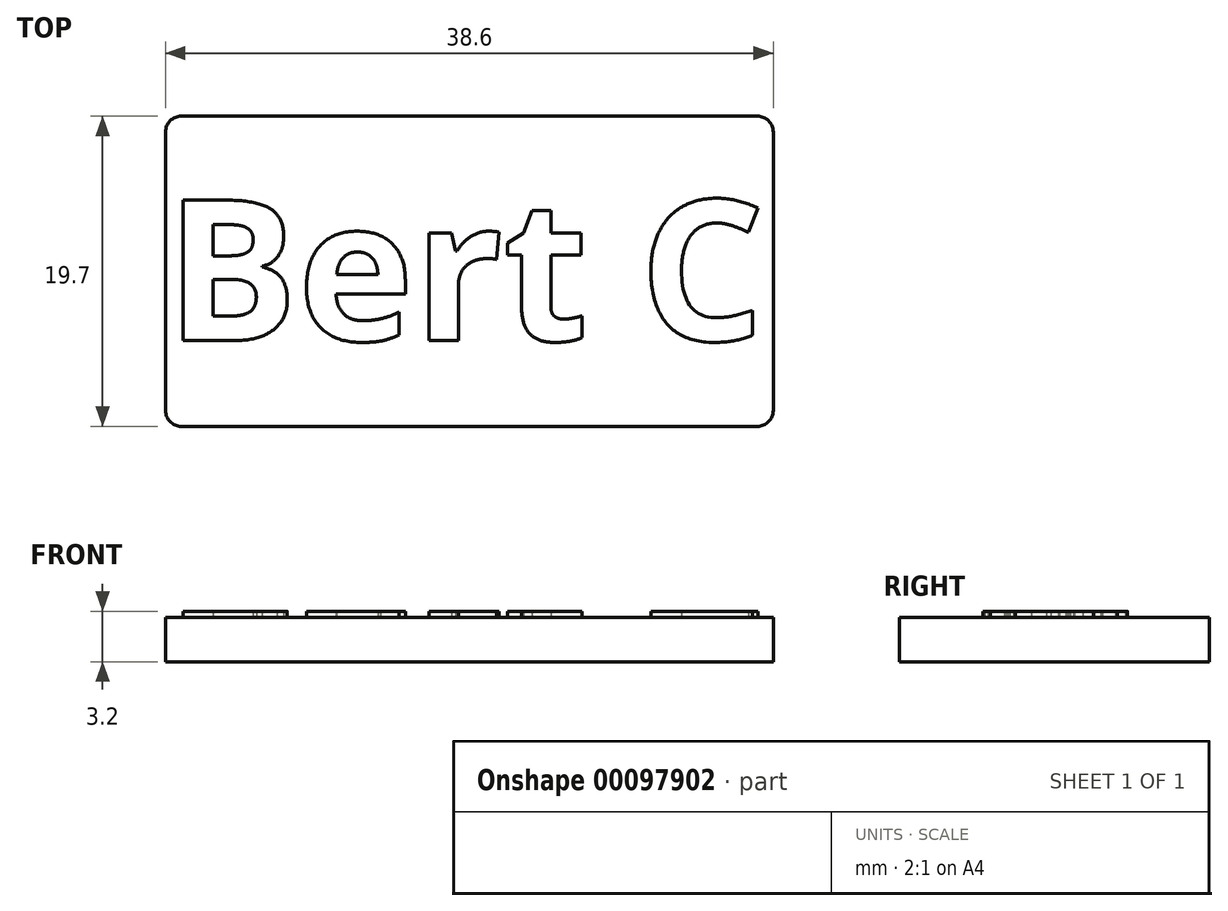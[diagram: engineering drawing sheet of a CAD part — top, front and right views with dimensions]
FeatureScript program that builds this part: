
annotation { "Feature Type Name" : "Feature", "Feature Type Description" : "" }
export const myFeature = defineFeature(function(context is Context, id is Id, definition is map)
    precondition{}
    {
        {
            var Q0;
            Q0=qCreatedBy(makeId("Top.planeOp"),FACE);
            var sketch = newSketch(context, id + "F0", { "sketchPlane" : qUnion([Q0])});
            skLineSegment(sketch, "E0.bottom", {"start": v(-23.84, 19.7) * mm, "end": v(14.76, 19.7) * mm});
            skLineSegment(sketch, "E0.top", {"start": v(-23.84, 0) * mm, "end": v(14.76, 0) * mm});
            skLineSegment(sketch, "E0.left", {"start": v(-23.84, 19.7) * mm, "end": v(-23.84, 0) * mm});
            skLineSegment(sketch, "E0.right", {"start": v(14.76, 19.7) * mm, "end": v(14.76, 0) * mm});
            skText(sketch, "E1", { "text": "Bert C\n", "fontName": "OpenSans-Bold.ttf"});
            const initialGuessF0  = {"E1": [-0.02384, 0.00545, 1, 0, 0.00899]};
            skSetInitialGuess(sketch, initialGuessF0);
            skSolve(sketch);
        }
        {
            var Q0;
            Q0=makeQuery(id+"F0.imprint","IMPRINT",FACE,{"disambiguationData":[TD([[makeQuery(id+"F0.imprint","IMPRINT",EDGE,{"derivedFrom":sQuery(id+"F0.wireOp",EDGE,"E0.bottom")}),-1.0]])]});
            var Q1;
            Q1=makeQuery(id+"F0.imprint","IMPRINT",FACE,{"disambiguationData":[TD([[makeQuery(id+"F0.imprint","IMPRINT",EDGE,{"derivedFrom":sQuery(id+"F0.wireOp",EDGE,"E1.sketch_text.stroke-0")}),-1.0]])]});
            var Q2;
            Q2=makeQuery(id+"F0.imprint","IMPRINT",FACE,{"disambiguationData":[TD([[makeQuery(id+"F0.imprint","IMPRINT",EDGE,{"derivedFrom":sQuery(id+"F0.wireOp",EDGE,"E1.sketch_text.stroke-12")}),1.0]])]});
            var Q3;
            Q3=makeQuery(id+"F0.imprint","IMPRINT",FACE,{"disambiguationData":[TD([[makeQuery(id+"F0.imprint","IMPRINT",EDGE,{"derivedFrom":sQuery(id+"F0.wireOp",EDGE,"E1.sketch_text.stroke-25")}),-1.0]])]});
            var Q4;
            Q4=makeQuery(id+"F0.imprint","IMPRINT",FACE,{"disambiguationData":[TD([[makeQuery(id+"F0.imprint","IMPRINT",EDGE,{"derivedFrom":sQuery(id+"F0.wireOp",EDGE,"E1.sketch_text.stroke-45")}),-1.0]])]});
            var Q5;
            Q5=makeQuery(id+"F0.imprint","IMPRINT",FACE,{"disambiguationData":[TD([[makeQuery(id+"F0.imprint","IMPRINT",EDGE,{"derivedFrom":sQuery(id+"F0.wireOp",EDGE,"E1.sketch_text.stroke-19")}),1.0]])]});
            var Q6;
            Q6=makeQuery(id+"F0.imprint","IMPRINT",FACE,{"disambiguationData":[TD([[makeQuery(id+"F0.imprint","IMPRINT",EDGE,{"derivedFrom":sQuery(id+"F0.wireOp",EDGE,"E1.sketch_text.stroke-25")}),1.0]])]});
            var Q7;
            Q7=makeQuery(id+"F0.imprint","IMPRINT",FACE,{"disambiguationData":[TD([[makeQuery(id+"F0.imprint","IMPRINT",EDGE,{"derivedFrom":sQuery(id+"F0.wireOp",EDGE,"E1.sketch_text.stroke-58")}),-1.0]])]});
            var Q8;
            Q8=makeQuery(id+"F0.imprint","IMPRINT",FACE,{"disambiguationData":[TD([[makeQuery(id+"F0.imprint","IMPRINT",EDGE,{"derivedFrom":sQuery(id+"F0.wireOp",EDGE,"E1.sketch_text.stroke-76")}),-1.0]])]});
            var Q9;
            Q9=sQuery(id+"F0.wireOp",EDGE,"E0.right");
            var Q10;
            Q10=sQuery(id+"F0.wireOp",EDGE,"E0.left");
            var Q11;
            Q11=sQuery(id+"F0.wireOp",EDGE,"E0.top");
            var Q12;
            Q12=sQuery(id+"F0.wireOp",EDGE,"E0.bottom");
            extrude(context, id + "F1", {"entities" : qUnion([Q0, Q1, Q2, Q3, Q4, Q5, Q6, Q7, Q8]), "surfaceEntities" : qUnion([Q9, Q10, Q11, Q12]), "depth" : 2.8 * mm});
        }
        {
            var Q0;
            Q0=makeQuery(id+"F0.imprint","IMPRINT",FACE,{"disambiguationData":[TD([[makeQuery(id+"F0.imprint","IMPRINT",EDGE,{"derivedFrom":sQuery(id+"F0.wireOp",EDGE,"E1.sketch_text.stroke-76")}),-1.0]])]});
            var Q1;
            Q1=makeQuery(id+"F0.imprint","IMPRINT",FACE,{"disambiguationData":[TD([[makeQuery(id+"F0.imprint","IMPRINT",EDGE,{"derivedFrom":sQuery(id+"F0.wireOp",EDGE,"E1.sketch_text.stroke-58")}),-1.0]])]});
            var Q2;
            Q2=makeQuery(id+"F0.imprint","IMPRINT",FACE,{"disambiguationData":[TD([[makeQuery(id+"F0.imprint","IMPRINT",EDGE,{"derivedFrom":sQuery(id+"F0.wireOp",EDGE,"E1.sketch_text.stroke-45")}),-1.0]])]});
            var Q3;
            Q3=makeQuery(id+"F0.imprint","IMPRINT",FACE,{"disambiguationData":[TD([[makeQuery(id+"F0.imprint","IMPRINT",EDGE,{"derivedFrom":sQuery(id+"F0.wireOp",EDGE,"E1.sketch_text.stroke-25")}),-1.0]])]});
            var Q4;
            Q4=makeQuery(id+"F0.imprint","IMPRINT",FACE,{"disambiguationData":[TD([[makeQuery(id+"F0.imprint","IMPRINT",EDGE,{"derivedFrom":sQuery(id+"F0.wireOp",EDGE,"E1.sketch_text.stroke-0")}),-1.0]])]});
            extrude(context, id + "F2", {"entities" : qUnion([Q0, Q1, Q2, Q3, Q4]), "operationType" : NewBodyOperationType.ADD, "depth" : 3.2 * mm});
        }
        {
            var Q0;
            Q0=makeQuery(id+"F1.opExtrude","SWEPT_EDGE",EDGE,{"disambiguationData":[OSD([sQuery(id+"F0.wireOp",EDGE,"E0.top"),sQuery(id+"F0.wireOp",EDGE,"E0.right")])]});
            var Q1;
            Q1=makeQuery(id+"F1.opExtrude","SWEPT_EDGE",EDGE,{"disambiguationData":[OSD([sQuery(id+"F0.wireOp",EDGE,"E0.bottom"),sQuery(id+"F0.wireOp",EDGE,"E0.right")])]});
            var Q2;
            Q2=makeQuery(id+"F1.opExtrude","SWEPT_EDGE",EDGE,{"disambiguationData":[OSD([sQuery(id+"F0.wireOp",EDGE,"E0.top"),sQuery(id+"F0.wireOp",EDGE,"E0.left")])]});
            var Q3;
            Q3=makeQuery(id+"F1.opExtrude","SWEPT_EDGE",EDGE,{"disambiguationData":[OSD([sQuery(id+"F0.wireOp",EDGE,"E0.bottom"),sQuery(id+"F0.wireOp",EDGE,"E0.left")])]});
            fillet(context, id + "F3", {"entities" : qUnion([Q0, Q1, Q2, Q3]), "radius" : 1 * mm, "tangentPropagation" : true, "allowEdgeOverflow" : false});
        }
    });
